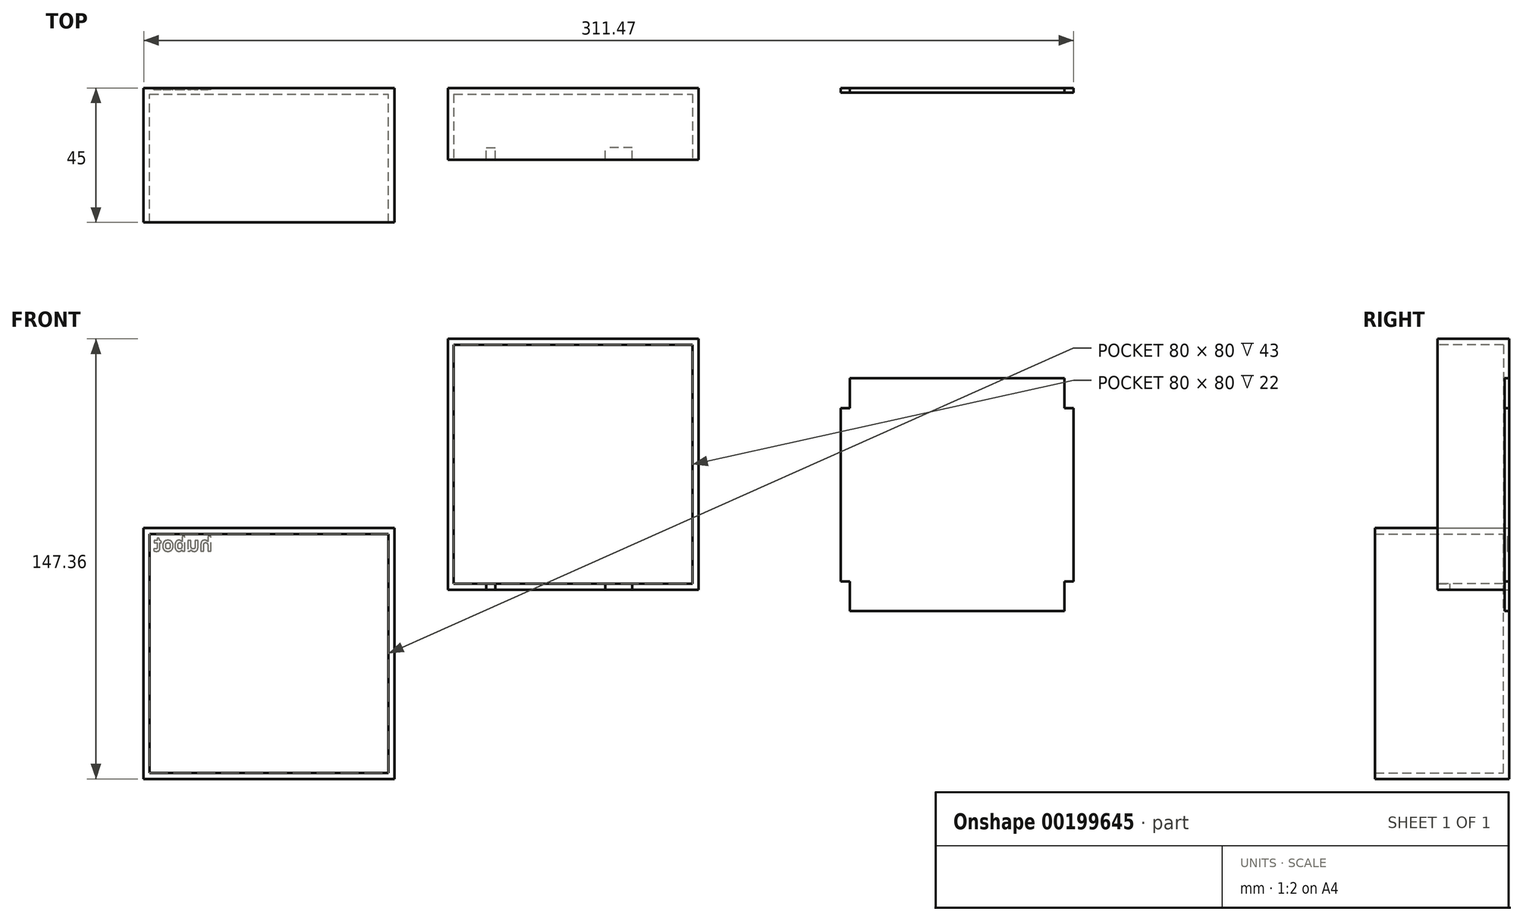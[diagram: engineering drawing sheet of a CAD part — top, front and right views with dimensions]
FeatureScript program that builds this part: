
annotation { "Feature Type Name" : "Feature", "Feature Type Description" : "" }
export const myFeature = defineFeature(function(context is Context, id is Id, definition is map)
    precondition{}
    {
        {
            var Q0;
            Q0=qCreatedBy(makeId("Front.planeOp"),FACE);
            var sketch = newSketch(context, id + "F0", { "sketchPlane" : qUnion([Q0])});
            skLineSegment(sketch, "E0.bottom", {"start": v(-42, 42) * mm, "end": v(42, 42) * mm});
            skLineSegment(sketch, "E0.top", {"start": v(-42, -42) * mm, "end": v(42, -42) * mm});
            skLineSegment(sketch, "E0.left", {"start": v(-42, 42) * mm, "end": v(-42, -42) * mm});
            skLineSegment(sketch, "E0.right", {"start": v(42, 42) * mm, "end": v(42, -42) * mm});
            skPoint(sketch, "E0.middle", {"position": v(0, 0) * mm});
            skSolve(sketch);
        }
        {
            var Q0;
            Q0 = qSketchRegion(id + "F0", true);
            extrude(context, id + "F1", {"entities" : qUnion([Q0]), "depth" : 24 * mm, "offsetDistance" : 25 * mm});
        }
        {
            var Q0;
            Q0=makeQuery(id+"F1.opExtrude","CAP_FACE",FACE,{"disambiguationData":[OSD([sQuery(id+"F0.wireOp",EDGE,"E0.bottom"),sQuery(id+"F0.wireOp",EDGE,"E0.top"),sQuery(id+"F0.wireOp",EDGE,"E0.left"),sQuery(id+"F0.wireOp",EDGE,"E0.right")])],"isStart":false});
            var sketch = newSketch(context, id + "F2", { "sketchPlane" : qUnion([Q0])});
            skLineSegment(sketch, "E1.bottom", {"start": v(-40, 40) * mm, "end": v(40, 40) * mm});
            skLineSegment(sketch, "E1.top", {"start": v(-40, -40) * mm, "end": v(40, -40) * mm});
            skLineSegment(sketch, "E1.left", {"start": v(-40, 40) * mm, "end": v(-40, -40) * mm});
            skLineSegment(sketch, "E1.right", {"start": v(40, 40) * mm, "end": v(40, -40) * mm});
            skPoint(sketch, "E1.middle", {"position": v(0, 0) * mm});
            skSolve(sketch);
        }
        {
            var Q0;
            Q0 = qSketchRegion(id + "F2", true);
            extrude(context, id + "F3", {"entities" : qUnion([Q0]), "operationType" : NewBodyOperationType.REMOVE, "oppositeDirection" : true, "depth" : 22 * mm, "offsetDistance" : 25 * mm});
        }
        {
            var Q0;
            Q0=makeQuery(id+"F1.opExtrude","SWEPT_FACE",FACE,{"disambiguationData":[OSD([sQuery(id+"F0.wireOp",EDGE,"E0.top")])]});
            var sketch = newSketch(context, id + "F4", { "sketchPlane" : qUnion([Q0])});
            skLineSegment(sketch, "E2.bottom", {"start": v(19.8, 24) * mm, "end": v(10.8, 24) * mm});
            skLineSegment(sketch, "E2.top", {"start": v(19.8, 20) * mm, "end": v(10.8, 20) * mm});
            skLineSegment(sketch, "E2.left", {"start": v(19.8, 24) * mm, "end": v(19.8, 20) * mm});
            skLineSegment(sketch, "E2.right", {"start": v(10.8, 24) * mm, "end": v(10.8, 20) * mm});
            skLineSegment(sketch, "E3.bottom", {"start": v(-29.1, 24) * mm, "end": v(-26.1, 24) * mm});
            skLineSegment(sketch, "E3.top", {"start": v(-29.1, 20) * mm, "end": v(-26.1, 20) * mm});
            skLineSegment(sketch, "E3.left", {"start": v(-29.1, 24) * mm, "end": v(-29.1, 20) * mm});
            skLineSegment(sketch, "E3.right", {"start": v(-26.1, 24) * mm, "end": v(-26.1, 20) * mm});
            skSolve(sketch);
        }
        {
            var Q0;
            Q0=makeQuery(id+"F4.imprint","IMPRINT",FACE,{"disambiguationData":[TD([[makeQuery(id+"F4.imprint","IMPRINT",EDGE,{"derivedFrom":sQuery(id+"F4.wireOp",EDGE,"E3.bottom")}),-1.0]])]});
            var Q1;
            Q1=makeQuery(id+"F4.imprint","IMPRINT",FACE,{"disambiguationData":[TD([[makeQuery(id+"F4.imprint","IMPRINT",EDGE,{"derivedFrom":sQuery(id+"F4.wireOp",EDGE,"E2.bottom")}),-1.0]])]});
            extrude(context, id + "F5", {"entities" : qUnion([Q0, Q1]), "operationType" : NewBodyOperationType.REMOVE, "oppositeDirection" : true, "depth" : 2.5 * mm, "offsetDistance" : 25 * mm});
        }
        {
            var Q0;
            Q0=qCreatedBy(makeId("Front.planeOp"),FACE);
            var sketch = newSketch(context, id + "F6", { "sketchPlane" : qUnion([Q0])});
            skLineSegment(sketch, "E4.bottom", {"start": v(92.6, 28.8) * mm, "end": v(164.6, 28.8) * mm});
            skLineSegment(sketch, "E4.top", {"start": v(92.6, -49.2) * mm, "end": v(164.6, -49.2) * mm});
            skLineSegment(sketch, "E4.left", {"start": v(89.6, 18.8) * mm, "end": v(89.6, -39.2) * mm});
            skLineSegment(sketch, "E4.right", {"start": v(167.6, 18.8) * mm, "end": v(167.6, -39.2) * mm});
            skLineSegment(sketch, "E5.top", {"start": v(89.6, 18.8) * mm, "end": v(92.6, 18.8) * mm});
            skLineSegment(sketch, "E5.right", {"start": v(92.6, 28.8) * mm, "end": v(92.6, 18.8) * mm});
            skLineSegment(sketch, "E6.top", {"start": v(167.6, 18.8) * mm, "end": v(164.6, 18.8) * mm});
            skLineSegment(sketch, "E6.right", {"start": v(164.6, 28.8) * mm, "end": v(164.6, 18.8) * mm});
            skLineSegment(sketch, "E7.top", {"start": v(167.6, -39.2) * mm, "end": v(164.6, -39.2) * mm});
            skLineSegment(sketch, "E7.right", {"start": v(164.6, -49.2) * mm, "end": v(164.6, -39.2) * mm});
            skLineSegment(sketch, "E8.top", {"start": v(89.6, -39.2) * mm, "end": v(92.6, -39.2) * mm});
            skLineSegment(sketch, "E8.right", {"start": v(92.6, -49.2) * mm, "end": v(92.6, -39.2) * mm});
            skSolve(sketch);
        }
        {
            var Q0;
            Q0 = qSketchRegion(id + "F6", true);
            extrude(context, id + "F7", {"entities" : qUnion([Q0]), "depth" : 1.6 * mm, "offsetDistance" : 25 * mm});
        }
        {
            var Q0;
            Q0=qCreatedBy(makeId("Front.planeOp"),FACE);
            var sketch = newSketch(context, id + "F8", { "sketchPlane" : qUnion([Q0])});
            skLineSegment(sketch, "E9.bottom", {"start": v(-143.87, -21.36) * mm, "end": v(-59.87, -21.36) * mm});
            skLineSegment(sketch, "E9.top", {"start": v(-143.87, -105.36) * mm, "end": v(-59.87, -105.36) * mm});
            skLineSegment(sketch, "E9.left", {"start": v(-143.87, -21.36) * mm, "end": v(-143.87, -105.36) * mm});
            skLineSegment(sketch, "E9.right", {"start": v(-59.87, -21.36) * mm, "end": v(-59.87, -105.36) * mm});
            skPoint(sketch, "E9.middle", {"position": v(-101.87, -63.36) * mm});
            skLineSegment(sketch, "E10.bottom", {"start": v(-61.87, -23.36) * mm, "end": v(-141.87, -23.36) * mm});
            skLineSegment(sketch, "E10.top", {"start": v(-61.87, -103.36) * mm, "end": v(-141.87, -103.36) * mm});
            skLineSegment(sketch, "E10.left", {"start": v(-61.87, -23.36) * mm, "end": v(-61.87, -103.36) * mm});
            skLineSegment(sketch, "E10.right", {"start": v(-141.87, -23.36) * mm, "end": v(-141.87, -103.36) * mm});
            skSolve(sketch);
        }
        {
            var Q0;
            Q0=makeQuery(id+"F8.imprint","IMPRINT",FACE,{"disambiguationData":[TD([[makeQuery(id+"F8.imprint","IMPRINT",EDGE,{"derivedFrom":sQuery(id+"F8.wireOp",EDGE,"E10.bottom")}),1.0]])]});
            var Q1;
            Q1=makeQuery(id+"F8.imprint","IMPRINT",FACE,{"disambiguationData":[TD([[makeQuery(id+"F8.imprint","IMPRINT",EDGE,{"derivedFrom":sQuery(id+"F8.wireOp",EDGE,"E9.bottom")}),-1.0]])]});
            extrude(context, id + "F9", {"entities" : qUnion([Q0, Q1]), "depth" : 2 * mm, "offsetDistance" : 25 * mm});
        }
        {
            var Q0;
            Q0 = qSketchRegion(id + "F8", true);
            extrude(context, id + "F10", {"entities" : qUnion([Q0]), "operationType" : NewBodyOperationType.ADD, "depth" : 45 * mm, "offsetDistance" : 25 * mm});
        }
        {
            var Q0;
            Q0=makeQuery(id+"F9.opExtrude","CAP_FACE",FACE,{"disambiguationData":[OSD([sQuery(id+"F8.wireOp",EDGE,"E9.bottom"),sQuery(id+"F8.wireOp",EDGE,"E9.top"),sQuery(id+"F8.wireOp",EDGE,"E9.left"),sQuery(id+"F8.wireOp",EDGE,"E9.right")])],"isStart":true});
            var sketch = newSketch(context, id + "F11", { "sketchPlane" : qUnion([Q0])});
            skText(sketch, "E11", { "text": "hubot", "fontName": "OpenSans-Bold.ttf"});
            const initialGuessF11  = {"E11": [0.12087, -0.0291, 1, 0, 0.00475]};
            skSetInitialGuess(sketch, initialGuessF11);
            skSolve(sketch);
        }
        {
            var Q0;
            Q0 = qSketchRegion(id + "F11", true);
            extrude(context, id + "F12", {"entities" : qUnion([Q0]), "operationType" : NewBodyOperationType.REMOVE, "oppositeDirection" : true, "depth" : 0.5 * mm, "offsetDistance" : 25 * mm});
        }
    });
